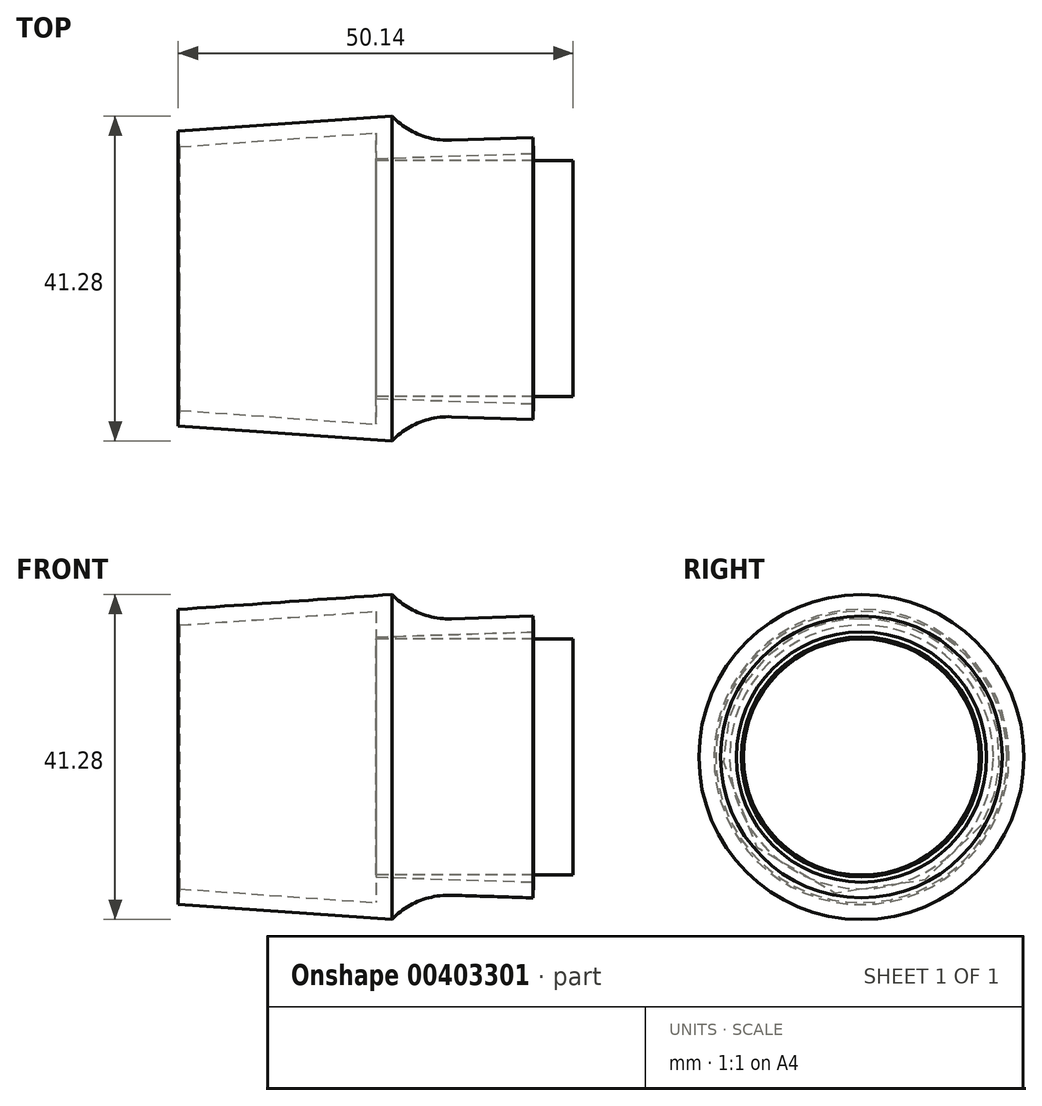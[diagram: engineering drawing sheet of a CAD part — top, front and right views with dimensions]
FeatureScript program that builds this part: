
annotation { "Feature Type Name" : "Feature", "Feature Type Description" : "" }
export const myFeature = defineFeature(function(context is Context, id is Id, definition is map)
    precondition{}
    {
        {
            var Q0;
            Q0=qCreatedBy(makeId("Front.planeOp"),FACE);
            var sketch = newSketch(context, id + "F0", { "sketchPlane" : qUnion([Q0])});
            skLineSegment(sketch, "E0", {"start": v(0, 15.25) * mm, "end": v(20, 15.9) * mm});
            skLineSegment(sketch, "E1", {"start": v(0, 18.5) * mm, "end": v(-25, 16.75) * mm});
            skLineSegment(sketch, "E2", {"start": v(0, 18.5) * mm, "end": v(0, 15.25) * mm});
            skLineSegment(sketch, "E3.0", {"start": v(2, 20.64) * mm, "end": v(-25.14, 18.75) * mm});
            skLineSegment(sketch, "E3.1", {"start": v(2, 20.64) * mm, "end": v(2, 17.32) * mm});
            skLineSegment(sketch, "E3.2", {"start": v(2, 17.32) * mm, "end": v(19.94, 17.9) * mm});
            skLineSegment(sketch, "E4", {"start": v(19.94, 17.9) * mm, "end": v(20, 15.9) * mm});
            skLineSegment(sketch, "E5", {"start": v(-25.14, 18.75) * mm, "end": v(-25, 16.75) * mm});
            skSolve(sketch);
        }
        {
            var Q0;
            Q0=qCreatedBy(makeId("Right.planeOp"),FACE);
            var sketch = newSketch(context, id + "F1", { "sketchPlane" : qUnion([Q0])});
            skCircle(sketch, "E6", {"center": v(0, 0) * mm, "radius": 15 * mm});
            skSolve(sketch);
        }
        {
            var Q0;
            Q0 = qSketchRegion(id + "F1", true);
            extrude(context, id + "F2", {"entities" : qUnion([Q0]), "depth" : 25 * mm});
        }
        {
            var Q0;
            Q0 = qSketchRegion(id + "F0", true);
            var Q1;
            Q1=makeQuery(id+"F2.opExtrude","CAP_EDGE",EDGE,{"disambiguationData":[OSD([sQuery(id+"F1.wireOp",EDGE,"E6")])],"isStart":true});
            sweep(context, id + "F3", {"profiles" : qUnion([Q0]), "path" : qUnion([Q1])});
        }
        {
            var Q0;
            Q0=makeQuery(id+"F3.opSweep","SWEPT_EDGE",EDGE,{"disambiguationData":[OSD([sQuery(id+"F0.wireOp",EDGE,"E3.1"),sQuery(id+"F0.wireOp",EDGE,"E3.2"),sQuery(id+"F1.wireOp",EDGE,"E6")])]});
            fillet(context, id + "F4", {"entities" : qUnion([Q0]), "radius" : 10 * mm, "tangentPropagation" : true, "allowEdgeOverflow" : false});
        }
    });
